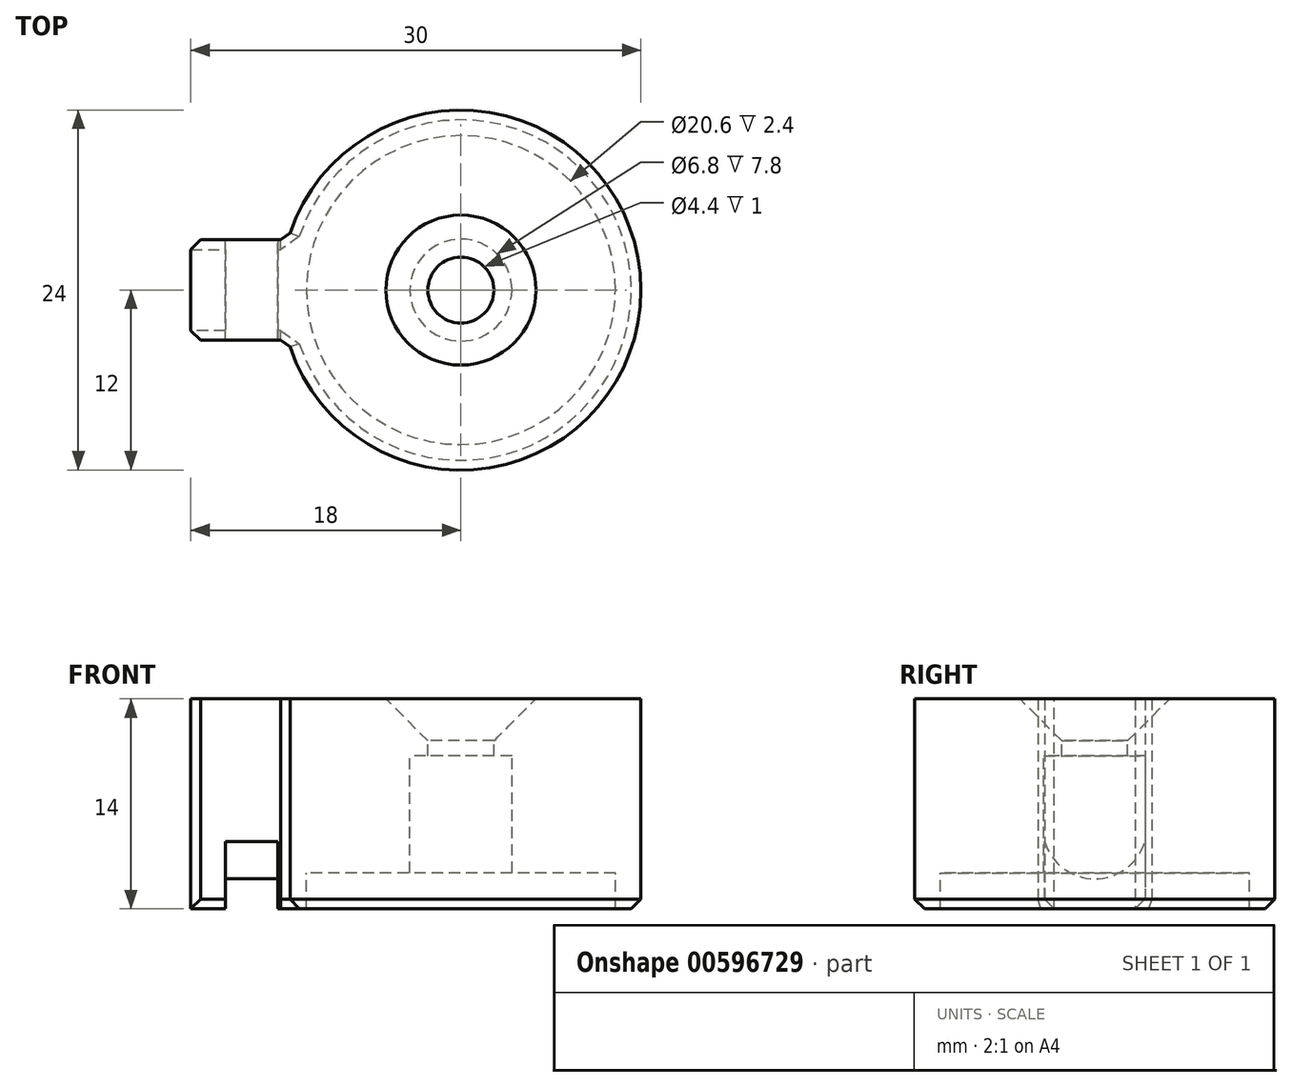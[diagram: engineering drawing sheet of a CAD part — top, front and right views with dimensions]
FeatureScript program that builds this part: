
annotation { "Feature Type Name" : "Feature", "Feature Type Description" : "" }
export const myFeature = defineFeature(function(context is Context, id is Id, definition is map)
    precondition{}
    {
        {
            var Q0;
            Q0=qCreatedBy(makeId("Top.planeOp"),FACE);
            var sketch = newSketch(context, id + "F0", { "sketchPlane" : qUnion([Q0])});
            skCircle(sketch, "E0", {"center": v(0, 0) * mm, "radius": 12 * mm});
            skLineSegment(sketch, "E1", {"start": v(-11.52, -3.35) * mm, "end": v(-18, -3.35) * mm});
            skLineSegment(sketch, "E2", {"start": v(-18, -3.35) * mm, "end": v(-18, 3.35) * mm});
            skLineSegment(sketch, "E3", {"start": v(-18, 3.35) * mm, "end": v(-11.52, 3.35) * mm});
            skLineSegment(sketch, "E4", {"start": v(-18, 0) * mm, "end": v(0, 0) * mm, "construction": true});
            skSolve(sketch);
        }
        {
            var Q0;
            Q0 = qSketchRegion(id + "F0", true);
            extrude(context, id + "F1", {"entities" : qUnion([Q0]), "depth" : 14 * mm, "offsetDistance" : 25 * mm});
        }
        {
            var Q0;
            Q0=qCreatedBy(makeId("Right.planeOp"),FACE);
            cPlane(context, id + "F2", {"entities" : qUnion([Q0]), "cplaneType" : CPlaneType.OFFSET, "offset" : 12.2 * mm, "oppositeDirection" : true, "width" : 150 * mm, "height" : 150 * mm});
        }
        {
            var Q0;
            Q0=qCreatedBy(id+"F2.planeOp",FACE);
            var sketch = newSketch(context, id + "F3", { "sketchPlane" : qUnion([Q0])});
            skArc(sketch, "E5", {"start": v(3.5, 5.5) * mm, "mid": v(0, 2) * mm, "end": v(-3.5, 5.5) * mm});
            skLineSegment(sketch, "E6", {"start": v(3.5, 5.5) * mm, "end": v(3.5, 0) * mm});
            skLineSegment(sketch, "E7", {"start": v(3.5, 0) * mm, "end": v(-3.5, 0) * mm});
            skLineSegment(sketch, "E8", {"start": v(-3.5, 0) * mm, "end": v(-3.5, 5.5) * mm});
            skLineSegment(sketch, "E9", {"start": v(3.93, 5.5) * mm, "end": v(0, 5.5) * mm, "construction": true});
            skLineSegment(sketch, "E10", {"start": v(-3.5, 5.5) * mm, "end": v(0, 5.5) * mm, "construction": true});
            skSolve(sketch);
        }
        {
            var Q0;
            Q0 = qSketchRegion(id + "F3", true);
            extrude(context, id + "F4", {"entities" : qUnion([Q0]), "operationType" : NewBodyOperationType.REMOVE, "oppositeDirection" : true, "depth" : 3.5 * mm, "offsetDistance" : 25 * mm});
        }
        {
            var Q0;
            Q0=qCreatedBy(makeId("Front.planeOp"),FACE);
            var sketch = newSketch(context, id + "F5", { "sketchPlane" : qUnion([Q0])});
            skLineSegment(sketch, "E11", {"start": v(0, 0) * mm, "end": v(0, 14.1) * mm});
            skLineSegment(sketch, "E12", {"start": v(0, 14.1) * mm, "end": v(5.1, 14.1) * mm});
            skLineSegment(sketch, "E13", {"start": v(5.1, 14.1) * mm, "end": v(2.2, 11.2) * mm});
            skLineSegment(sketch, "E14", {"start": v(2.2, 11.2) * mm, "end": v(2.2, 10.2) * mm});
            skLineSegment(sketch, "E15", {"start": v(2.2, 10.2) * mm, "end": v(3.4, 10.2) * mm});
            skLineSegment(sketch, "E16", {"start": v(3.4, 10.2) * mm, "end": v(3.4, 2.4) * mm});
            skLineSegment(sketch, "E17", {"start": v(3.4, 2.4) * mm, "end": v(10.3, 2.4) * mm});
            skLineSegment(sketch, "E18", {"start": v(10.3, 2.4) * mm, "end": v(10.3, 0) * mm});
            skLineSegment(sketch, "E19", {"start": v(10.3, 0) * mm, "end": v(0, 0) * mm});
            skSolve(sketch);
        }
        {
            var Q0;
            Q0 = qSketchRegion(id + "F5", true);
            var Q1;
            Q1=sQuery(id+"F5.wireOp",EDGE,"E11");
            revolve(context, id + "F6", {"operationType" : NewBodyOperationType.REMOVE, "entities" : qUnion([Q0]), "axis" : qUnion([Q1]), "revolveType" : RevolveType.FULL, "oppositeDirection" : true});
        }
        {
            var Q0;
            Q0=makeQuery(id+"F1.opExtrude","SWEPT_EDGE",EDGE,{"disambiguationData":[OSD([sQuery(id+"F0.wireOp",EDGE,"E0"),sQuery(id+"F0.wireOp",EDGE,"E1")])]});
            var Q1;
            {var subQ0=sQuery(id+"F0.wireOp",EDGE,"E0");var subQ1=sQuery(id+"F0.wireOp",EDGE,"E1");Q1=makeQuery(id+"F4.boolean.opBoolean","SPLIT",EDGE,{"disambiguationData":[TD([makeQuery(id+"F1.opExtrude","SWEPT_FACE",FACE,{"disambiguationData":[OSD([subQ0])]})])],"derivedFrom":makeQuery(id+"F1.opExtrude","CAP_EDGE",EDGE,{"disambiguationData":[OSD([subQ1])],"isStart":true})});}
            var Q2;
            {var subQ0=sQuery(id+"F0.wireOp",EDGE,"E0");var subQ1=sQuery(id+"F0.wireOp",EDGE,"E3");Q2=makeQuery(id+"F4.boolean.opBoolean","SPLIT",EDGE,{"disambiguationData":[TD([makeQuery(id+"F1.opExtrude","SWEPT_FACE",FACE,{"disambiguationData":[OSD([subQ0])]})])],"derivedFrom":makeQuery(id+"F1.opExtrude","CAP_EDGE",EDGE,{"disambiguationData":[OSD([subQ1])],"isStart":true})});}
            var Q3;
            Q3=makeQuery(id+"F1.opExtrude","SWEPT_EDGE",EDGE,{"disambiguationData":[OSD([sQuery(id+"F0.wireOp",EDGE,"E1"),sQuery(id+"F0.wireOp",EDGE,"E2")])]});
            var Q4;
            Q4=makeQuery(id+"F1.opExtrude","SWEPT_EDGE",EDGE,{"disambiguationData":[OSD([sQuery(id+"F0.wireOp",EDGE,"E2"),sQuery(id+"F0.wireOp",EDGE,"E3")])]});
            var Q5;
            {var subQ0=sQuery(id+"F0.wireOp",EDGE,"E2");var subQ1=sQuery(id+"F0.wireOp",EDGE,"E1");Q5=makeQuery(id+"F4.boolean.opBoolean","SPLIT",EDGE,{"disambiguationData":[TD([makeQuery(id+"F1.opExtrude","SWEPT_FACE",FACE,{"disambiguationData":[OSD([subQ0])]})])],"derivedFrom":makeQuery(id+"F1.opExtrude","CAP_EDGE",EDGE,{"disambiguationData":[OSD([subQ1])],"isStart":true})});}
            var Q6;
            {var subQ0=sQuery(id+"F0.wireOp",EDGE,"E3");var subQ1=sQuery(id+"F0.wireOp",EDGE,"E2");Q6=makeQuery(id+"F4.boolean.opBoolean","SPLIT",EDGE,{"disambiguationData":[TD([makeQuery(id+"F1.opExtrude","SWEPT_FACE",FACE,{"disambiguationData":[OSD([subQ1])]})])],"derivedFrom":makeQuery(id+"F1.opExtrude","CAP_EDGE",EDGE,{"disambiguationData":[OSD([subQ0])],"isStart":true})});}
            var Q7;
            Q7=makeQuery(id+"F1.opExtrude","SWEPT_EDGE",EDGE,{"disambiguationData":[OSD([sQuery(id+"F0.wireOp",EDGE,"E0"),sQuery(id+"F0.wireOp",EDGE,"E3")])]});
            chamfer(context, id + "F7", {"entities" : qUnion([Q0, Q1, Q2, Q3, Q4, Q5, Q6, Q7]), "width" : 0.65 * mm, "tangentPropagation" : true});
        }
    });
